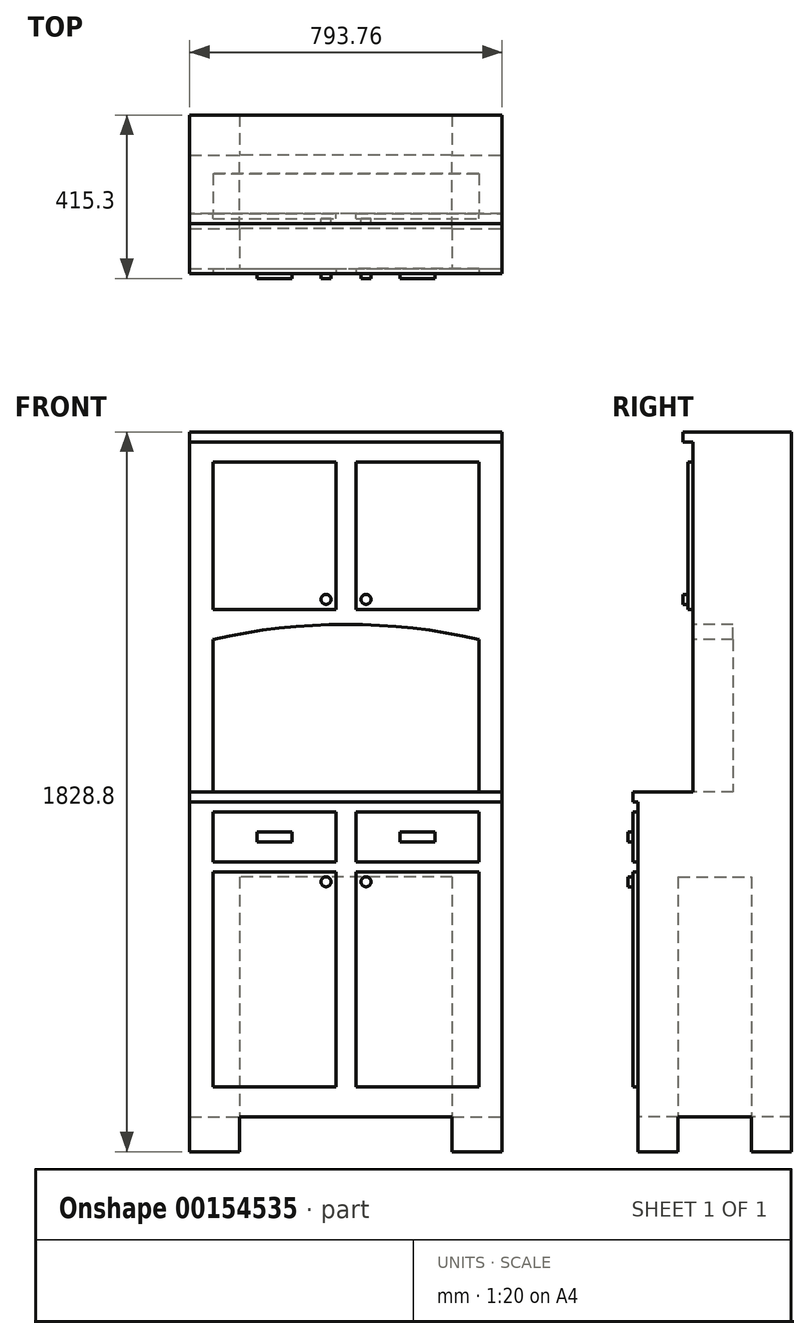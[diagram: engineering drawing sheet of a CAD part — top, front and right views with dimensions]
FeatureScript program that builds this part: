
annotation { "Feature Type Name" : "Feature", "Feature Type Description" : "" }
export const myFeature = defineFeature(function(context is Context, id is Id, definition is map)
    precondition{}
    {
        {
            var Q0;
            Q0=qCreatedBy(makeId("Top.planeOp"),FACE);
            var sketch = newSketch(context, id + "F0", { "sketchPlane" : qUnion([Q0])});
            skLineSegment(sketch, "E0.bottom", {"start": v(-396.88, 201.3) * mm, "end": v(396.88, 201.3) * mm});
            skLineSegment(sketch, "E0.top", {"start": v(-396.88, -201.3) * mm, "end": v(396.88, -201.3) * mm});
            skLineSegment(sketch, "E0.left", {"start": v(-396.88, 201.3) * mm, "end": v(-396.88, -201.3) * mm});
            skLineSegment(sketch, "E0.right", {"start": v(396.88, 201.3) * mm, "end": v(396.88, -201.3) * mm});
            skPoint(sketch, "E0.middle", {"position": v(0, 0) * mm});
            skSolve(sketch);
        }
        {
            var Q0;
            Q0=makeQuery(id+"F0.imprint","IMPRINT",FACE,{"disambiguationData":[TD([[makeQuery(id+"F0.imprint","IMPRINT",EDGE,{"derivedFrom":sQuery(id+"F0.wireOp",EDGE,"E0.bottom")}),-1.0]])]});
            extrude(context, id + "F1", {"entities" : qUnion([Q0]), "depth" : 1828.8 * mm});
        }
        {
            var Q0;
            Q0=makeQuery(id+"F1.opExtrude","SWEPT_FACE",FACE,{"disambiguationData":[OSD([sQuery(id+"F0.wireOp",EDGE,"E0.top")])]});
            var sketch = newSketch(context, id + "F2", { "sketchPlane" : qUnion([Q0])});
            skLineSegment(sketch, "E1.bottom", {"start": v(-269.87, 0) * mm, "end": v(269.88, 0) * mm});
            skLineSegment(sketch, "E1.top", {"start": v(-269.88, 88.9) * mm, "end": v(269.88, 88.9) * mm});
            skLineSegment(sketch, "E1.left", {"start": v(-269.87, 0) * mm, "end": v(-269.87, 88.9) * mm});
            skLineSegment(sketch, "E1.right", {"start": v(269.88, 0) * mm, "end": v(269.88, 88.9) * mm});
            skLineSegment(sketch, "E2.bottom", {"start": v(-396.88, 1828.8) * mm, "end": v(396.88, 1828.8) * mm});
            skLineSegment(sketch, "E2.top", {"start": v(-396.88, 0) * mm, "end": v(396.88, 0) * mm});
            skLineSegment(sketch, "E2.left", {"start": v(-396.88, 1828.8) * mm, "end": v(-396.88, 0) * mm});
            skLineSegment(sketch, "E2.right", {"start": v(396.88, 1828.8) * mm, "end": v(396.88, 0) * mm});
            skLineSegment(sketch, "E3.bottom", {"start": v(-338.2, 711.2) * mm, "end": v(-25.4, 711.2) * mm});
            skLineSegment(sketch, "E3.top", {"start": v(-338.2, 165.1) * mm, "end": v(-25.4, 165.1) * mm});
            skLineSegment(sketch, "E3.left", {"start": v(-338.2, 711.2) * mm, "end": v(-338.2, 165.1) * mm});
            skLineSegment(sketch, "E3.right", {"start": v(-25.4, 711.2) * mm, "end": v(-25.4, 165.1) * mm});
            skLineSegment(sketch, "E4.bottom", {"start": v(25.4, 711.2) * mm, "end": v(338.2, 711.2) * mm});
            skLineSegment(sketch, "E4.top", {"start": v(25.4, 165.1) * mm, "end": v(338.2, 165.1) * mm});
            skLineSegment(sketch, "E4.left", {"start": v(25.4, 711.2) * mm, "end": v(25.4, 165.1) * mm});
            skLineSegment(sketch, "E4.right", {"start": v(338.2, 711.2) * mm, "end": v(338.2, 165.1) * mm});
            skLineSegment(sketch, "E5.bottom", {"start": v(-338.2, 863.6) * mm, "end": v(-25.4, 863.6) * mm});
            skLineSegment(sketch, "E5.top", {"start": v(-338.2, 736.6) * mm, "end": v(-25.4, 736.6) * mm});
            skLineSegment(sketch, "E5.left", {"start": v(-338.2, 863.6) * mm, "end": v(-338.2, 736.6) * mm});
            skLineSegment(sketch, "E5.right", {"start": v(-25.4, 863.6) * mm, "end": v(-25.4, 736.6) * mm});
            skLineSegment(sketch, "E6.bottom", {"start": v(-338.2, 1301.75) * mm, "end": v(338.2, 1301.75) * mm});
            skLineSegment(sketch, "E6.top", {"start": v(-338.2, 914.4) * mm, "end": v(338.2, 914.4) * mm});
            skLineSegment(sketch, "E6.left", {"start": v(-338.2, 1301.75) * mm, "end": v(-338.2, 914.4) * mm});
            skLineSegment(sketch, "E6.right", {"start": v(338.2, 1301.75) * mm, "end": v(338.2, 914.4) * mm});
            skLineSegment(sketch, "E7.bottom", {"start": v(338.2, 863.6) * mm, "end": v(25.4, 863.6) * mm});
            skLineSegment(sketch, "E7.top", {"start": v(338.2, 736.6) * mm, "end": v(25.4, 736.6) * mm});
            skLineSegment(sketch, "E7.left", {"start": v(338.2, 863.6) * mm, "end": v(338.2, 736.6) * mm});
            skLineSegment(sketch, "E7.right", {"start": v(25.4, 863.6) * mm, "end": v(25.4, 736.6) * mm});
            skLineSegment(sketch, "E8", {"start": v(-25.4, 165.1) * mm, "end": v(25.4, 165.1) * mm, "construction": true});
            skLineSegment(sketch, "E9", {"start": v(0, 88.9) * mm, "end": v(0, 165.1) * mm, "construction": true});
            skLineSegment(sketch, "E10.bottom", {"start": v(-396.88, 914.4) * mm, "end": v(396.88, 914.4) * mm});
            skLineSegment(sketch, "E10.top", {"start": v(-396.88, 889) * mm, "end": v(396.88, 889) * mm});
            skLineSegment(sketch, "E10.left", {"start": v(-396.88, 914.4) * mm, "end": v(-396.88, 889) * mm});
            skLineSegment(sketch, "E10.right", {"start": v(396.88, 914.4) * mm, "end": v(396.88, 889) * mm});
            skLineSegment(sketch, "E11.bottom", {"start": v(-338.2, 1752.6) * mm, "end": v(-25.4, 1752.6) * mm});
            skLineSegment(sketch, "E11.top", {"start": v(-338.2, 1377.95) * mm, "end": v(-25.4, 1377.95) * mm});
            skLineSegment(sketch, "E11.left", {"start": v(-338.2, 1752.6) * mm, "end": v(-338.2, 1377.95) * mm});
            skLineSegment(sketch, "E11.right", {"start": v(-25.4, 1752.6) * mm, "end": v(-25.4, 1377.95) * mm});
            skLineSegment(sketch, "E12.bottom", {"start": v(338.2, 1752.6) * mm, "end": v(25.4, 1752.6) * mm});
            skLineSegment(sketch, "E12.top", {"start": v(338.2, 1377.95) * mm, "end": v(25.4, 1377.95) * mm});
            skLineSegment(sketch, "E12.left", {"start": v(338.2, 1752.6) * mm, "end": v(338.2, 1377.95) * mm});
            skLineSegment(sketch, "E12.right", {"start": v(25.4, 1752.6) * mm, "end": v(25.4, 1377.95) * mm});
            skArc(sketch, "E13", {"start": v(338.2, 1301.75) * mm, "mid": v(0, 1339.75) * mm, "end": v(-338.2, 1301.75) * mm});
            skPoint(sketch, "E13.third.point", {"position": v(1502.74, 69.44) * mm});
            skSolve(sketch);
        }
        {
            var Q0;
            Q0=makeQuery(id+"F2.imprint","IMPRINT",FACE,{"disambiguationData":[TD([[makeQuery(id+"F2.imprint","IMPRINT",EDGE,{"derivedFrom":sQuery(id+"F2.wireOp",EDGE,"E1.top")}),-1.0]])]});
            extrude(context, id + "F3", {"entities" : qUnion([Q0]), "operationType" : NewBodyOperationType.REMOVE, "endBound" : BoundingType.THROUGH_ALL, "oppositeDirection" : true, "depth" : 30.48 * mm});
        }
        {
            var Q0;
            Q0=makeQuery(id+"F2.imprint","IMPRINT",FACE,{"disambiguationData":[TD([[makeQuery(id+"F2.imprint","IMPRINT",EDGE,{"derivedFrom":sQuery(id+"F2.wireOp",EDGE,"E1.top")}),1.0]])]});
            extrude(context, id + "F4", {"entities" : qUnion([Q0]), "operationType" : NewBodyOperationType.REMOVE, "oppositeDirection" : true, "depth" : 12.7 * mm});
        }
        {
            var Q0;
            {var subQ7=sQuery(id+"F2.wireOp",EDGE,"E2.bottom");Q0=makeQuery(id+"F2.imprint","IMPRINT",FACE,{"disambiguationData":[TD([[makeQuery(id+"F2.imprint","IMPRINT",EDGE,{"derivedFrom":subQ7}),-1.0]])]});}
            var Q1;
            Q1=makeQuery(id+"F2.imprint","IMPRINT",FACE,{"disambiguationData":[TD([[makeQuery(id+"F2.imprint","IMPRINT",EDGE,{"derivedFrom":sQuery(id+"F2.wireOp",EDGE,"E11.bottom")}),-1.0]])]});
            var Q2;
            Q2=makeQuery(id+"F2.imprint","IMPRINT",FACE,{"disambiguationData":[TD([[makeQuery(id+"F2.imprint","IMPRINT",EDGE,{"derivedFrom":sQuery(id+"F2.wireOp",EDGE,"E12.bottom")}),1.0]])]});
            var Q3;
            Q3=makeQuery(id+"F2.imprint","IMPRINT",FACE,{"disambiguationData":[TD([[makeQuery(id+"F2.imprint","IMPRINT",EDGE,{"derivedFrom":sQuery(id+"F2.wireOp",EDGE,"E6.bottom")}),-1.0]])]});
            extrude(context, id + "F5", {"entities" : qUnion([Q0, Q1, Q2, Q3]), "operationType" : NewBodyOperationType.REMOVE, "oppositeDirection" : true, "depth" : 152.4 * mm});
        }
        {
            var Q0;
            Q0=makeQuery(id+"F2.imprint","IMPRINT",FACE,{"disambiguationData":[TD([[makeQuery(id+"F2.imprint","IMPRINT",EDGE,{"derivedFrom":sQuery(id+"F2.wireOp",EDGE,"E6.bottom")}),-1.0]])]});
            var Q1;
            Q1=makeQuery(id+"F2.imprint","IMPRINT",FACE,{"disambiguationData":[TD([[makeQuery(id+"F2.imprint","IMPRINT",EDGE,{"derivedFrom":sQuery(id+"F2.wireOp",EDGE,"E6.bottom")}),1.0]])]});
            extrude(context, id + "F6", {"entities" : qUnion([Q0, Q1]), "operationType" : NewBodyOperationType.REMOVE, "oppositeDirection" : true, "depth" : 254 * mm});
        }
        {
            var Q0;
            Q0=makeQuery(id+"F5.boolean.opBoolean","COPY",FACE,{"derivedFrom":makeQuery(id+"F5.opExtrude","CAP_FACE",FACE,{"disambiguationData":[OSD([sQuery(id+"F2.wireOp",EDGE,"E2.bottom"),sQuery(id+"F2.wireOp",EDGE,"E2.left"),sQuery(id+"F2.wireOp",EDGE,"E2.right"),sQuery(id+"F2.wireOp",EDGE,"E6.bottom"),sQuery(id+"F2.wireOp",EDGE,"E10.bottom"),sQuery(id+"F2.wireOp",EDGE,"E13")])],"isStart":false})});
            var sketch = newSketch(context, id + "F7", { "sketchPlane" : qUnion([Q0])});
            skLineSegment(sketch, "E14.bottom", {"start": v(-338.2, 1752.6) * mm, "end": v(-25.4, 1752.6) * mm});
            skLineSegment(sketch, "E14.top", {"start": v(-338.2, 1377.95) * mm, "end": v(-25.4, 1377.95) * mm});
            skLineSegment(sketch, "E14.left", {"start": v(-338.2, 1752.6) * mm, "end": v(-338.2, 1377.95) * mm});
            skLineSegment(sketch, "E14.right", {"start": v(-25.4, 1752.6) * mm, "end": v(-25.4, 1377.95) * mm});
            skLineSegment(sketch, "E15.bottom", {"start": v(25.4, 1752.6) * mm, "end": v(338.2, 1752.6) * mm});
            skLineSegment(sketch, "E15.top", {"start": v(25.4, 1377.95) * mm, "end": v(338.2, 1377.95) * mm});
            skLineSegment(sketch, "E15.left", {"start": v(25.4, 1752.6) * mm, "end": v(25.4, 1377.95) * mm});
            skLineSegment(sketch, "E15.right", {"start": v(338.2, 1752.6) * mm, "end": v(338.2, 1377.95) * mm});
            skSolve(sketch);
        }
        {
            var Q0;
            Q0=makeQuery(id+"F7.imprint","IMPRINT",FACE,{"disambiguationData":[TD([[makeQuery(id+"F7.imprint","IMPRINT",EDGE,{"derivedFrom":sQuery(id+"F7.wireOp",EDGE,"E15.bottom")}),-1.0]])]});
            var Q1;
            Q1=makeQuery(id+"F7.imprint","IMPRINT",FACE,{"disambiguationData":[TD([[makeQuery(id+"F7.imprint","IMPRINT",EDGE,{"derivedFrom":sQuery(id+"F7.wireOp",EDGE,"E14.bottom")}),-1.0]])]});
            extrude(context, id + "F8", {"entities" : qUnion([Q0, Q1]), "operationType" : NewBodyOperationType.ADD, "depth" : 12.7 * mm});
        }
        {
            var Q0;
            Q0=makeQuery(id+"F1.opExtrude","SWEPT_FACE",FACE,{"disambiguationData":[OSD([sQuery(id+"F0.wireOp",EDGE,"E0.right")])]});
            var sketch = newSketch(context, id + "F9", { "sketchPlane" : qUnion([Q0])});
            skLineSegment(sketch, "E16.bottom", {"start": v(99.7, 0) * mm, "end": v(-87, 0) * mm});
            skLineSegment(sketch, "E16.top", {"start": v(99.7, 88.9) * mm, "end": v(-87, 88.9) * mm});
            skLineSegment(sketch, "E16.left", {"start": v(99.7, 0) * mm, "end": v(99.7, 88.9) * mm});
            skLineSegment(sketch, "E16.right", {"start": v(-87, 0) * mm, "end": v(-87, 88.9) * mm});
            skSolve(sketch);
        }
        {
            var Q0;
            Q0=makeQuery(id+"F9.imprint","IMPRINT",FACE,{"disambiguationData":[TD([[makeQuery(id+"F9.imprint","IMPRINT",EDGE,{"derivedFrom":sQuery(id+"F9.wireOp",EDGE,"E16.bottom")}),-1.0]])]});
            extrude(context, id + "F10", {"entities" : qUnion([Q0]), "operationType" : NewBodyOperationType.REMOVE, "endBound" : BoundingType.THROUGH_ALL, "oppositeDirection" : true, "depth" : 30.48 * mm});
        }
        {
            var Q0;
            Q0=makeQuery(id+"F4.boolean.opBoolean","SPLIT",FACE,{"disambiguationData":[TD([makeQuery(id+"F4.opExtrude","SWEPT_FACE",FACE,{"disambiguationData":[OSD([sQuery(id+"F2.wireOp",EDGE,"E5.bottom")])]})])],"derivedFrom":makeQuery(id+"F1.opExtrude","SWEPT_FACE",FACE,{"disambiguationData":[OSD([sQuery(id+"F0.wireOp",EDGE,"E0.top")])]})});
            var sketch = newSketch(context, id + "F11", { "sketchPlane" : qUnion([Q0])});
            skCircle(sketch, "E17", {"center": v(-50.8, 685.8) * mm, "radius": 12.7 * mm});
            skCircle(sketch, "E18", {"center": v(50.8, 685.8) * mm, "radius": 12.7 * mm});
            skLineSegment(sketch, "E19.bottom", {"start": v(-226.25, 812.8) * mm, "end": v(-137.35, 812.8) * mm});
            skLineSegment(sketch, "E19.top", {"start": v(-226.25, 787.4) * mm, "end": v(-137.35, 787.4) * mm});
            skLineSegment(sketch, "E19.left", {"start": v(-226.25, 812.8) * mm, "end": v(-226.25, 787.4) * mm});
            skLineSegment(sketch, "E19.right", {"start": v(-137.35, 812.8) * mm, "end": v(-137.35, 787.4) * mm});
            skLineSegment(sketch, "E20.bottom", {"start": v(137.26, 812.8) * mm, "end": v(226.16, 812.8) * mm});
            skLineSegment(sketch, "E20.top", {"start": v(137.26, 787.4) * mm, "end": v(226.16, 787.4) * mm});
            skLineSegment(sketch, "E20.left", {"start": v(137.26, 812.8) * mm, "end": v(137.26, 787.4) * mm});
            skLineSegment(sketch, "E20.right", {"start": v(226.16, 812.8) * mm, "end": v(226.16, 787.4) * mm});
            skCircle(sketch, "E21", {"center": v(50.8, 1403.35) * mm, "radius": 12.7 * mm});
            skCircle(sketch, "E22", {"center": v(-50.8, 1403.35) * mm, "radius": 12.7 * mm});
            skLineSegment(sketch, "E23", {"start": v(-181.8, 787.4) * mm, "end": v(-181.8, 736.6) * mm, "construction": true});
            skLineSegment(sketch, "E24", {"start": v(-338.2, 800.1) * mm, "end": v(-226.25, 800.1) * mm, "construction": true});
            skPoint(sketch, "E24.endSnap0", {"position": v(-226.25, 800.1) * mm});
            skSolve(sketch);
        }
        {
            var Q0;
            Q0=makeQuery(id+"F11.imprint","IMPRINT",FACE,{"disambiguationData":[TD([[makeQuery(id+"F11.imprint","IMPRINT",EDGE,{"derivedFrom":sQuery(id+"F11.wireOp",EDGE,"E20.bottom")}),-1.0]])]});
            var Q1;
            Q1=makeQuery(id+"F11.imprint","IMPRINT",FACE,{"disambiguationData":[TD([[makeQuery(id+"F11.imprint","IMPRINT",EDGE,{"derivedFrom":sQuery(id+"F11.wireOp",EDGE,"E18")}),1.0]])]});
            var Q2;
            Q2=makeQuery(id+"F11.imprint","IMPRINT",FACE,{"disambiguationData":[TD([[makeQuery(id+"F11.imprint","IMPRINT",EDGE,{"derivedFrom":sQuery(id+"F11.wireOp",EDGE,"E17")}),1.0]])]});
            var Q3;
            Q3=makeQuery(id+"F11.imprint","IMPRINT",FACE,{"disambiguationData":[TD([[makeQuery(id+"F11.imprint","IMPRINT",EDGE,{"derivedFrom":sQuery(id+"F11.wireOp",EDGE,"E19.bottom")}),-1.0]])]});
            extrude(context, id + "F12", {"entities" : qUnion([Q0, Q1, Q2, Q3]), "operationType" : NewBodyOperationType.ADD, "depth" : 12.7 * mm});
        }
        {
            var Q0;
            Q0=makeQuery(id+"F8.opExtrude","CAP_FACE",FACE,{"disambiguationData":[OSD([sQuery(id+"F7.wireOp",EDGE,"E14.bottom"),sQuery(id+"F7.wireOp",EDGE,"E14.top"),sQuery(id+"F7.wireOp",EDGE,"E14.left"),sQuery(id+"F7.wireOp",EDGE,"E14.right")])],"isStart":false});
            var sketch = newSketch(context, id + "F13", { "sketchPlane" : qUnion([Q0])});
            skCircle(sketch, "E25", {"center": v(-50.8, 1403.35) * mm, "radius": 12.7 * mm});
            skCircle(sketch, "E26", {"center": v(50.8, 1403.35) * mm, "radius": 12.7 * mm});
            skSolve(sketch);
        }
        {
            var Q0;
            Q0 = qSketchRegion(id + "F13", true);
            extrude(context, id + "F14", {"entities" : qUnion([Q0]), "operationType" : NewBodyOperationType.ADD, "depth" : 12.7 * mm});
        }
        {
            var Q0;
            Q0=makeQuery(id+"F1.opExtrude","CAP_FACE",FACE,{"disambiguationData":[OSD([sQuery(id+"F0.wireOp",EDGE,"E0.bottom"),sQuery(id+"F0.wireOp",EDGE,"E0.top"),sQuery(id+"F0.wireOp",EDGE,"E0.left"),sQuery(id+"F0.wireOp",EDGE,"E0.right")])],"isStart":false});
            var sketch = newSketch(context, id + "F15", { "sketchPlane" : qUnion([Q0])});
            skLineSegment(sketch, "E27.bottom", {"start": v(-396.88, 201.3) * mm, "end": v(396.88, 201.3) * mm});
            skLineSegment(sketch, "E27.top", {"start": v(-396.88, -74.3) * mm, "end": v(396.88, -74.3) * mm});
            skLineSegment(sketch, "E27.left", {"start": v(-396.88, 201.3) * mm, "end": v(-396.88, -74.3) * mm});
            skLineSegment(sketch, "E27.right", {"start": v(396.88, 201.3) * mm, "end": v(396.88, -74.3) * mm});
            skSolve(sketch);
        }
        {
            var Q0;
            {var subQ0=sQuery(id+"F15.wireOp",EDGE,"E27.bottom");Q0=makeQuery(id+"F15.imprint","IMPRINT",FACE,{"disambiguationData":[TD([[makeQuery(id+"F15.imprint","IMPRINT",EDGE,{"derivedFrom":subQ0}),-1.0]])]});}
            var Q1;
            {var subQ0=sQuery(id+"F15.wireOp",EDGE,"E27.top");Q1=makeQuery(id+"F15.imprint","IMPRINT",FACE,{"disambiguationData":[TD([[makeQuery(id+"F15.imprint","IMPRINT",EDGE,{"derivedFrom":subQ0}),1.0]])]});}
            extrude(context, id + "F16", {"entities" : qUnion([Q0, Q1]), "operationType" : NewBodyOperationType.ADD, "oppositeDirection" : true, "depth" : 25.4 * mm});
        }
        {
            var Q0;
            Q0=makeQuery(id+"F10.boolean.opBoolean","MERGE",FACE,{"derivedFrom":[makeQuery(id+"F3.boolean.opBoolean","COPY",FACE,{"derivedFrom":makeQuery(id+"F3.opExtrude","SWEPT_FACE",FACE,{"disambiguationData":[OSD([sQuery(id+"F2.wireOp",EDGE,"E1.top")])]})}),makeQuery(id+"F10.opExtrude","SWEPT_FACE",FACE,{"disambiguationData":[OSD([sQuery(id+"F9.wireOp",EDGE,"E16.top")])]})]});
            var sketch = newSketch(context, id + "F17", { "sketchPlane" : qUnion([Q0])});
            skLineSegment(sketch, "E28.bottom", {"start": v(269.87, 87) * mm, "end": v(-269.87, 87) * mm});
            skLineSegment(sketch, "E28.top", {"start": v(269.87, -99.7) * mm, "end": v(-269.87, -99.7) * mm});
            skLineSegment(sketch, "E28.left", {"start": v(269.87, 87) * mm, "end": v(269.87, -99.7) * mm});
            skLineSegment(sketch, "E28.right", {"start": v(-269.87, 87) * mm, "end": v(-269.87, -99.7) * mm});
            skSolve(sketch);
        }
        {
            var Q0;
            Q0=makeQuery(id+"F17.imprint","IMPRINT",FACE,{"disambiguationData":[TD([[makeQuery(id+"F17.imprint","IMPRINT",EDGE,{"derivedFrom":sQuery(id+"F17.wireOp",EDGE,"E28.bottom")}),1.0]])]});
            extrude(context, id + "F18", {"entities" : qUnion([Q0]), "operationType" : NewBodyOperationType.REMOVE, "oppositeDirection" : true, "depth" : 609.6 * mm});
        }
    });
